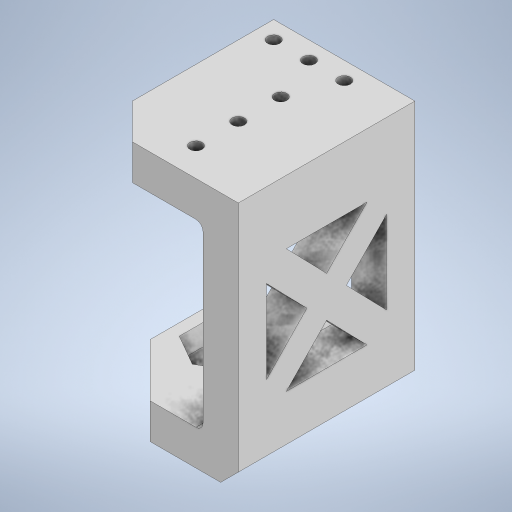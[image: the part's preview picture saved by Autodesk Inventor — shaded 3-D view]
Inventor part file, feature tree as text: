
AUTODESK INVENTOR PART (.ipt)
format: ipt  version: 2023 (Build 270158000, 158)  size: 326,656 bytes
history: native  units: mm
features: extrude x7, sketch x6, chamfer x3, other x2, fillet x1, projected_geometry x1
ambient origin geometry x8: Origin, YZ Plane, XZ Plane, XY Plane, X Axis, Y Axis, Z Axis, Center Point
bodies: Body1 (feature_tree)
feature tree (20):
  other  "솔리드1"
  extrude  "돌출1"  Depth=71.0mm
  other  "작업 평면1"
  extrude  "돌출5"  Depth=10.0mm
  fillet  "모깎기1"  Radius=10.0mm
  extrude  "돌출6"  Depth=30.0mm
  chamfer  "모따기1"  Distance=50.0mm
  extrude  "돌출7"  Depth=6.0mm
  sketch  "스케치14"
  extrude  "돌출12"  Depth=8.0mm
  extrude  "돌출13"  Depth=4.0mm
  extrude  "돌출14"  Depth=4.0mm
  chamfer  "모따기3"  Distance=10.0mm
  chamfer  "모따기4"  Distance=2.0mm
  sketch  "스케치1"
  sketch  "스케치5"
  projected_geometry  "투영된 루프1"
  sketch  "스케치6"
  sketch  "스케치7"
  sketch  "스케치15"
